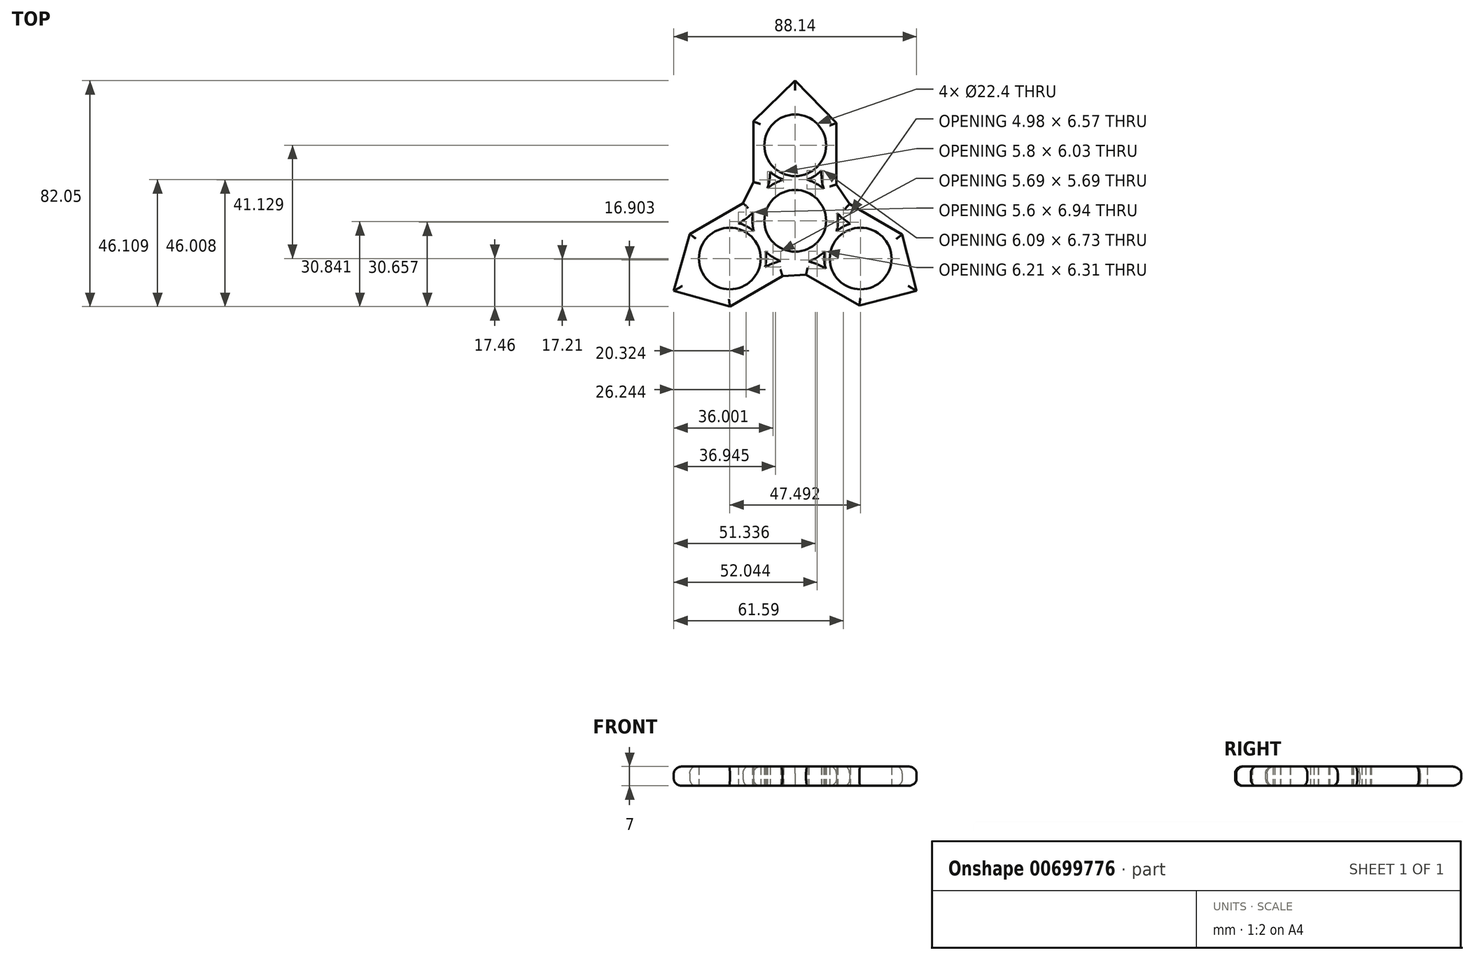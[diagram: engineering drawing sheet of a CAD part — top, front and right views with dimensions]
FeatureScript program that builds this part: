
annotation { "Feature Type Name" : "Feature", "Feature Type Description" : "" }
export const myFeature = defineFeature(function(context is Context, id is Id, definition is map)
    precondition{}
    {
        {
            var Q0;
            Q0=qCreatedBy(makeId("Top.planeOp"),FACE);
            var sketch = newSketch(context, id + "F0", { "sketchPlane" : qUnion([Q0])});
            skCircle(sketch, "E0", {"center": v(0, 0) * mm, "radius": 11.2 * mm});
            skArc(sketch, "E1", {"start": v(-4.22, 14.91) * mm, "mid": v(-7.3, 13.68) * mm, "end": v(-10.03, 11.82) * mm});
            skCircle(sketch, "E2", {"center": v(0, 27.42) * mm, "radius": 11.2 * mm});
            skArc(sketch, "E3", {"start": v(4.22, 14.91) * mm, "mid": v(0, 40.62) * mm, "end": v(-4.22, 14.91) * mm});
            skArc(sketch, "E4.1.0", {"start": v(-15.03, -3.8) * mm, "mid": v(-35.18, -20.3) * mm, "end": v(-10.8, -11.11) * mm});
            skCircle(sketch, "E4.1.1", {"center": v(-23.75, -13.7) * mm, "radius": 11.2 * mm});
            skArc(sketch, "E4.2.0", {"start": v(10.8, -11.11) * mm, "mid": v(35.18, -20.3) * mm, "end": v(15.03, -3.8) * mm});
            skCircle(sketch, "E4.2.1", {"center": v(23.75, -13.7) * mm, "radius": 11.2 * mm});
            skArc(sketch, "E5", {"start": v(9.55, 18.3) * mm, "mid": v(9.66, 14.9) * mm, "end": v(10.3, 11.57) * mm});
            skArc(sketch, "E6.1.0", {"start": v(-20.63, -0.88) * mm, "mid": v(-17.74, 0.91) * mm, "end": v(-15.18, 3.14) * mm});
            skArc(sketch, "E6.2.0", {"start": v(11.08, -17.42) * mm, "mid": v(8.08, -15.82) * mm, "end": v(4.87, -14.72) * mm});
            skLineSegment(sketch, "E7", {"start": v(-15.14, 14.04) * mm, "end": v(-15.14, 36.11) * mm});
            skLineSegment(sketch, "E8", {"start": v(-15.14, 36.11) * mm, "end": v(0, 50.88) * mm});
            skLineSegment(sketch, "E9", {"start": v(0, 50.88) * mm, "end": v(14.97, 35.53) * mm});
            skLineSegment(sketch, "E10", {"start": v(14.97, 35.53) * mm, "end": v(14.97, 13.2) * mm});
            skLineSegment(sketch, "E11.1.0", {"start": v(-23.7, -31.17) * mm, "end": v(-44.07, -25.44) * mm});
            skLineSegment(sketch, "E11.1.1", {"start": v(-44.07, -25.44) * mm, "end": v(-38.26, -4.8) * mm});
            skLineSegment(sketch, "E11.1.2", {"start": v(-4.59, -20.13) * mm, "end": v(-23.7, -31.17) * mm});
            skLineSegment(sketch, "E11.1.3", {"start": v(-38.26, -4.8) * mm, "end": v(-18.92, 6.37) * mm});
            skLineSegment(sketch, "E11.2.0", {"start": v(38.85, -4.95) * mm, "end": v(44.07, -25.44) * mm});
            skLineSegment(sketch, "E11.2.1", {"start": v(44.07, -25.44) * mm, "end": v(23.29, -30.73) * mm});
            skLineSegment(sketch, "E11.2.2", {"start": v(19.73, 6.1) * mm, "end": v(38.85, -4.95) * mm});
            skLineSegment(sketch, "E11.2.3", {"start": v(23.29, -30.73) * mm, "end": v(3.94, -19.57) * mm});
            skLineSegment(sketch, "E12", {"start": v(-4.59, -20.13) * mm, "end": v(3.94, -19.57) * mm});
            skLineSegment(sketch, "E13", {"start": v(-18.92, 6.37) * mm, "end": v(-15.14, 14.04) * mm});
            skLineSegment(sketch, "E14", {"start": v(14.97, 13.2) * mm, "end": v(19.73, 6.1) * mm});
            skArc(sketch, "E15.trimOffspring", {"start": v(-10.03, 11.82) * mm, "mid": v(-9.34, 14.8) * mm, "end": v(-9.1, 17.86) * mm});
            skArc(sketch, "E16.trimOffspring", {"start": v(-15.18, 3.14) * mm, "mid": v(-15.5, -0.34) * mm, "end": v(-15.03, -3.8) * mm});
            skArc(sketch, "E17.trimOffspring", {"start": v(-10.8, -11.11) * mm, "mid": v(-8.2, -13.15) * mm, "end": v(-5.22, -14.6) * mm});
            skArc(sketch, "E18.trimOffspring", {"start": v(-5.22, -14.6) * mm, "mid": v(-8.15, -15.5) * mm, "end": v(-10.91, -16.8) * mm});
            skArc(sketch, "E19.trimOffspring", {"start": v(4.87, -14.72) * mm, "mid": v(8.04, -13.25) * mm, "end": v(10.8, -11.11) * mm});
            skArc(sketch, "E20.trimOffspring", {"start": v(15.03, -3.8) * mm, "mid": v(15.5, -0.52) * mm, "end": v(15.25, 2.77) * mm});
            skArc(sketch, "E21.trimOffspring", {"start": v(10.3, 11.57) * mm, "mid": v(7.46, 13.59) * mm, "end": v(4.22, 14.91) * mm});
            skArc(sketch, "E22.trimOffspring", {"start": v(15.25, 2.77) * mm, "mid": v(17.5, 0.7) * mm, "end": v(20.01, -1.05) * mm});
            skSolve(sketch);
        }
        {
            var Q0;
            Q0 = qSketchRegion(id + "F0", true);
            extrude(context, id + "F1", {"entities" : qUnion([Q0]), "depth" : 7 * mm, "offsetDistance" : 25 * mm});
        }
        {
            var Q0;
            Q0=sQuery(id+"F0.wireOp",EDGE,"E9");
            var Q1;
            Q1=sQuery(id+"F0.wireOp",EDGE,"E8");
            var Q2;
            Q2=sQuery(id+"F0.wireOp",EDGE,"E7");
            var Q3;
            Q3=sQuery(id+"F0.wireOp",EDGE,"E10");
            var Q4;
            Q4=sQuery(id+"F0.wireOp",EDGE,"E11.2.2");
            var Q5;
            Q5=sQuery(id+"F0.wireOp",EDGE,"E11.2.0");
            var Q6;
            Q6=sQuery(id+"F0.wireOp",EDGE,"E11.2.1");
            var Q7;
            Q7=sQuery(id+"F0.wireOp",EDGE,"E11.2.3");
            var Q8;
            Q8=sQuery(id+"F0.wireOp",EDGE,"E11.1.2");
            var Q9;
            Q9=sQuery(id+"F0.wireOp",EDGE,"E11.1.0");
            var Q10;
            Q10=sQuery(id+"F0.wireOp",EDGE,"E11.1.1");
            var Q11;
            Q11=sQuery(id+"F0.wireOp",EDGE,"E11.1.3");
            extrude(context, id + "F2", {"bodyType" : ToolBodyType.SURFACE, "surfaceEntities" : qUnion([Q0, Q1, Q2, Q3, Q4, Q5, Q6, Q7, Q8, Q9, Q10, Q11]), "depth" : 7 * mm, "offsetDistance" : 25 * mm});
        }
        {
            var Q0;
            Q0 = qSketchRegion(id + "F0", true);
            extrude(context, id + "F3", {"entities" : qUnion([Q0]), "operationType" : NewBodyOperationType.ADD, "depth" : 7 * mm, "offsetDistance" : 25 * mm});
        }
        {
            var Q0;
            Q0 = qSketchRegion(id + "F0", true);
            var Q1;
            Q1=makeQuery(id+"F0.imprint","IMPRINT",FACE,{"disambiguationData":[TD([[makeQuery(id+"F0.imprint","IMPRINT",EDGE,{"derivedFrom":sQuery(id+"F0.wireOp",EDGE,"E0")}),-1.0]])]});
            var Q2;
            Q2=makeQuery(id+"F0.imprint","IMPRINT",FACE,{"disambiguationData":[TD([[makeQuery(id+"F0.imprint","IMPRINT",EDGE,{"derivedFrom":sQuery(id+"F0.wireOp",EDGE,"E2")}),-1.0]])]});
            var Q3;
            Q3=makeQuery(id+"F0.imprint","IMPRINT",FACE,{"disambiguationData":[TD([[makeQuery(id+"F0.imprint","IMPRINT",EDGE,{"derivedFrom":sQuery(id+"F0.wireOp",EDGE,"E4.1.1")}),-1.0]])]});
            var Q4;
            Q4=makeQuery(id+"F0.imprint","IMPRINT",FACE,{"disambiguationData":[TD([[makeQuery(id+"F0.imprint","IMPRINT",EDGE,{"derivedFrom":sQuery(id+"F0.wireOp",EDGE,"E4.2.1")}),-1.0]])]});
            extrude(context, id + "F4", {"entities" : qUnion([Q0, Q1, Q2, Q3, Q4]), "operationType" : NewBodyOperationType.ADD, "depth" : 7 * mm, "offsetDistance" : 25 * mm});
        }
        {
            var Q0;
            Q0=makeQuery(id+"F1.opExtrude","CAP_EDGE",EDGE,{"disambiguationData":[OSD([sQuery(id+"F0.wireOp",EDGE,"E8")])],"isStart":false});
            var Q1;
            Q1=makeQuery(id+"F1.opExtrude","CAP_EDGE",EDGE,{"disambiguationData":[OSD([sQuery(id+"F0.wireOp",EDGE,"E7")])],"isStart":false});
            var Q2;
            Q2=makeQuery(id+"F1.opExtrude","CAP_EDGE",EDGE,{"disambiguationData":[OSD([sQuery(id+"F0.wireOp",EDGE,"E13")])],"isStart":false});
            var Q3;
            Q3=makeQuery(id+"F1.opExtrude","CAP_EDGE",EDGE,{"disambiguationData":[OSD([sQuery(id+"F0.wireOp",EDGE,"E11.1.3")])],"isStart":false});
            var Q4;
            Q4=makeQuery(id+"F1.opExtrude","CAP_EDGE",EDGE,{"disambiguationData":[OSD([sQuery(id+"F0.wireOp",EDGE,"E11.1.1")])],"isStart":false});
            var Q5;
            Q5=makeQuery(id+"F1.opExtrude","CAP_EDGE",EDGE,{"disambiguationData":[OSD([sQuery(id+"F0.wireOp",EDGE,"E11.1.0")])],"isStart":false});
            var Q6;
            Q6=makeQuery(id+"F1.opExtrude","CAP_EDGE",EDGE,{"disambiguationData":[OSD([sQuery(id+"F0.wireOp",EDGE,"E11.1.2")])],"isStart":false});
            var Q7;
            Q7=makeQuery(id+"F1.opExtrude","CAP_EDGE",EDGE,{"disambiguationData":[OSD([sQuery(id+"F0.wireOp",EDGE,"E12")])],"isStart":false});
            var Q8;
            Q8=makeQuery(id+"F1.opExtrude","CAP_EDGE",EDGE,{"disambiguationData":[OSD([sQuery(id+"F0.wireOp",EDGE,"E11.2.3")])],"isStart":false});
            var Q9;
            Q9=makeQuery(id+"F1.opExtrude","CAP_EDGE",EDGE,{"disambiguationData":[OSD([sQuery(id+"F0.wireOp",EDGE,"E11.2.1")])],"isStart":false});
            var Q10;
            Q10=makeQuery(id+"F1.opExtrude","CAP_EDGE",EDGE,{"disambiguationData":[OSD([sQuery(id+"F0.wireOp",EDGE,"E11.2.0")])],"isStart":false});
            var Q11;
            Q11=makeQuery(id+"F1.opExtrude","CAP_EDGE",EDGE,{"disambiguationData":[OSD([sQuery(id+"F0.wireOp",EDGE,"E11.2.2")])],"isStart":false});
            var Q12;
            Q12=makeQuery(id+"F1.opExtrude","CAP_EDGE",EDGE,{"disambiguationData":[OSD([sQuery(id+"F0.wireOp",EDGE,"E14")])],"isStart":false});
            var Q13;
            Q13=makeQuery(id+"F1.opExtrude","CAP_EDGE",EDGE,{"disambiguationData":[OSD([sQuery(id+"F0.wireOp",EDGE,"E10")])],"isStart":false});
            var Q14;
            Q14=makeQuery(id+"F1.opExtrude","CAP_EDGE",EDGE,{"disambiguationData":[OSD([sQuery(id+"F0.wireOp",EDGE,"E9")])],"isStart":false});
            var Q15;
            Q15=makeQuery(id+"F1.opExtrude","CAP_EDGE",EDGE,{"disambiguationData":[OSD([sQuery(id+"F0.wireOp",EDGE,"E9")])],"isStart":true});
            var Q16;
            Q16=makeQuery(id+"F1.opExtrude","CAP_EDGE",EDGE,{"disambiguationData":[OSD([sQuery(id+"F0.wireOp",EDGE,"E8")])],"isStart":true});
            var Q17;
            Q17=makeQuery(id+"F1.opExtrude","CAP_EDGE",EDGE,{"disambiguationData":[OSD([sQuery(id+"F0.wireOp",EDGE,"E7")])],"isStart":true});
            var Q18;
            Q18=makeQuery(id+"F1.opExtrude","CAP_EDGE",EDGE,{"disambiguationData":[OSD([sQuery(id+"F0.wireOp",EDGE,"E13")])],"isStart":true});
            var Q19;
            Q19=makeQuery(id+"F1.opExtrude","CAP_EDGE",EDGE,{"disambiguationData":[OSD([sQuery(id+"F0.wireOp",EDGE,"E11.1.2")])],"isStart":true});
            var Q20;
            Q20=makeQuery(id+"F1.opExtrude","CAP_EDGE",EDGE,{"disambiguationData":[OSD([sQuery(id+"F0.wireOp",EDGE,"E12")])],"isStart":true});
            var Q21;
            Q21=makeQuery(id+"F1.opExtrude","CAP_EDGE",EDGE,{"disambiguationData":[OSD([sQuery(id+"F0.wireOp",EDGE,"E11.2.3")])],"isStart":true});
            var Q22;
            Q22=makeQuery(id+"F1.opExtrude","CAP_EDGE",EDGE,{"disambiguationData":[OSD([sQuery(id+"F0.wireOp",EDGE,"E11.2.1")])],"isStart":true});
            var Q23;
            Q23=makeQuery(id+"F1.opExtrude","CAP_EDGE",EDGE,{"disambiguationData":[OSD([sQuery(id+"F0.wireOp",EDGE,"E11.2.0")])],"isStart":true});
            var Q24;
            Q24=makeQuery(id+"F1.opExtrude","CAP_EDGE",EDGE,{"disambiguationData":[OSD([sQuery(id+"F0.wireOp",EDGE,"E11.2.2")])],"isStart":true});
            var Q25;
            Q25=makeQuery(id+"F1.opExtrude","CAP_EDGE",EDGE,{"disambiguationData":[OSD([sQuery(id+"F0.wireOp",EDGE,"E14")])],"isStart":true});
            var Q26;
            Q26=makeQuery(id+"F1.opExtrude","CAP_EDGE",EDGE,{"disambiguationData":[OSD([sQuery(id+"F0.wireOp",EDGE,"E10")])],"isStart":true});
            var Q27;
            Q27=makeQuery(id+"F1.opExtrude","CAP_EDGE",EDGE,{"disambiguationData":[OSD([sQuery(id+"F0.wireOp",EDGE,"E11.1.3")])],"isStart":true});
            var Q28;
            Q28=makeQuery(id+"F1.opExtrude","CAP_EDGE",EDGE,{"disambiguationData":[OSD([sQuery(id+"F0.wireOp",EDGE,"E11.1.1")])],"isStart":true});
            var Q29;
            Q29=makeQuery(id+"F1.opExtrude","CAP_EDGE",EDGE,{"disambiguationData":[OSD([sQuery(id+"F0.wireOp",EDGE,"E11.1.0")])],"isStart":true});
            fillet(context, id + "F5", {"entities" : qUnion([Q0, Q1, Q2, Q3, Q4, Q5, Q6, Q7, Q8, Q9, Q10, Q11, Q12, Q13, Q14, Q15, Q16, Q17, Q18, Q19, Q20, Q21, Q22, Q23, Q24, Q25, Q26, Q27, Q28, Q29]), "radius" : 2.5 * mm, "tangentPropagation" : true, "allowEdgeOverflow" : false});
        }
    });
